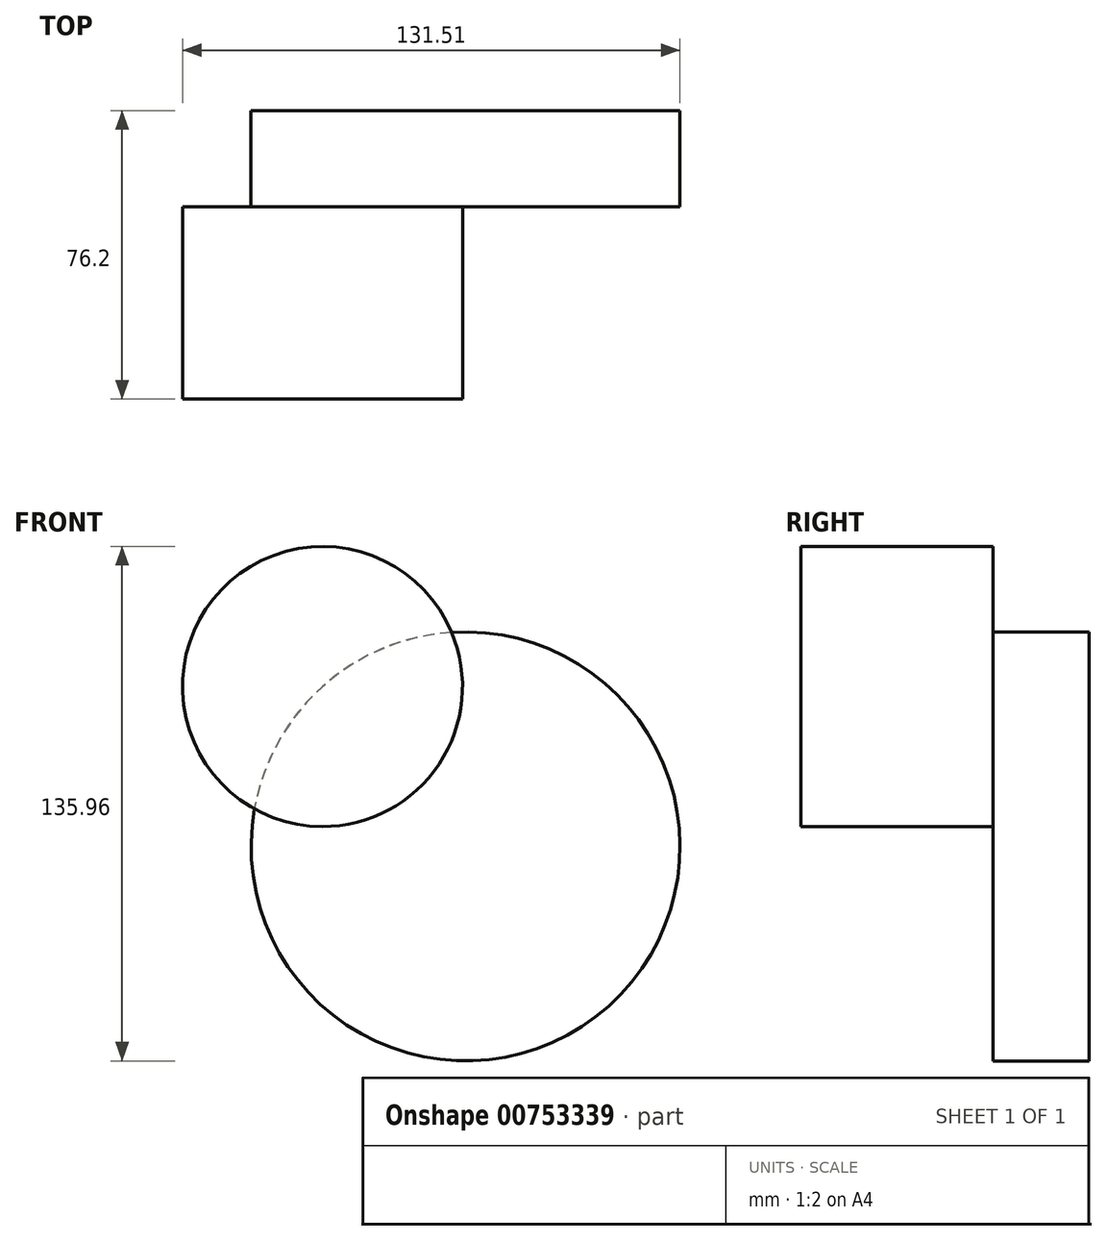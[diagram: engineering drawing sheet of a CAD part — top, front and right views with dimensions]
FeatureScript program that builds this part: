
annotation { "Feature Type Name" : "Feature", "Feature Type Description" : "" }
export const myFeature = defineFeature(function(context is Context, id is Id, definition is map)
    precondition{}
    {
        {
            var Q0;
            Q0=qCreatedBy(makeId("Front.planeOp"),FACE);
            var sketch = newSketch(context, id + "F0", { "sketchPlane" : qUnion([Q0])});
            skLineSegment(sketch, "E0.bottom", {"start": v(0, 0) * mm, "end": v(0, 0) * mm});
            skLineSegment(sketch, "E0.top", {"start": v(0, 0) * mm, "end": v(0, 0) * mm});
            skLineSegment(sketch, "E0.left", {"start": v(0, 0) * mm, "end": v(0, 0) * mm});
            skLineSegment(sketch, "E0.right", {"start": v(0, 0) * mm, "end": v(0, 0) * mm});
            skCircle(sketch, "E1", {"center": v(0, 23.6) * mm, "radius": 23.6 * mm});
            skSolve(sketch);
        }
        {
            var Q0;
            Q0 = qSketchRegion(id + "F0", true);
            var sketch = newSketch(context, id + "F1", { "sketchPlane" : qUnion([Q0])});
            skCircle(sketch, "E2", {"center": v(0, 18.8) * mm, "radius": 56.7 * mm});
            skSolve(sketch);
        }
        {
            var Q0;
            Q0 = qSketchRegion(id + "F1", true);
            extrude(context, id + "F2", {"entities" : qUnion([Q0]), "depth" : 25.4 * mm, "offsetDistance" : 25.4 * mm});
        }
        {
            var Q0;
            Q0=makeQuery(id+"F2.opExtrude","CAP_FACE",FACE,{"disambiguationData":[OSD([sQuery(id+"F1.wireOp",EDGE,"E2")])],"isStart":false});
            var sketch = newSketch(context, id + "F3", { "sketchPlane" : qUnion([Q0])});
            skCircle(sketch, "E3", {"center": v(-37.8, 61.04) * mm, "radius": 37.02 * mm});
            skSolve(sketch);
        }
        {
            var Q0;
            Q0 = qSketchRegion(id + "F3", true);
            extrude(context, id + "F4", {"entities" : qUnion([Q0]), "operationType" : NewBodyOperationType.ADD, "depth" : 25.4 * mm, "offsetDistance" : 25.4 * mm});
        }
        {
            var Q0;
            Q0=makeQuery(id+"F4.opExtrude","CAP_FACE",FACE,{"disambiguationData":[OSD([sQuery(id+"F3.wireOp",EDGE,"E3")])],"isStart":false});
            extrude(context, id + "F5", {"entities" : qUnion([Q0]), "operationType" : NewBodyOperationType.ADD, "depth" : 25.4 * mm, "offsetDistance" : 25.4 * mm});
        }
        {
            var Q0;
            Q0 = qSketchRegion(id + "F0", true);
            var sketch = newSketch(context, id + "F6", { "sketchPlane" : qUnion([Q0])});
            skCircle(sketch, "E4", {"center": v(0, 20.07) * mm, "radius": 26.87 * mm});
            skSolve(sketch);
        }
        {
            var Q0;
            Q0 = qSketchRegion(id + "F6", true);
            extrude(context, id + "F7", {"entities" : qUnion([Q0]), "operationType" : NewBodyOperationType.ADD, "depth" : 25.4 * mm, "offsetDistance" : 25.4 * mm});
        }
    });
